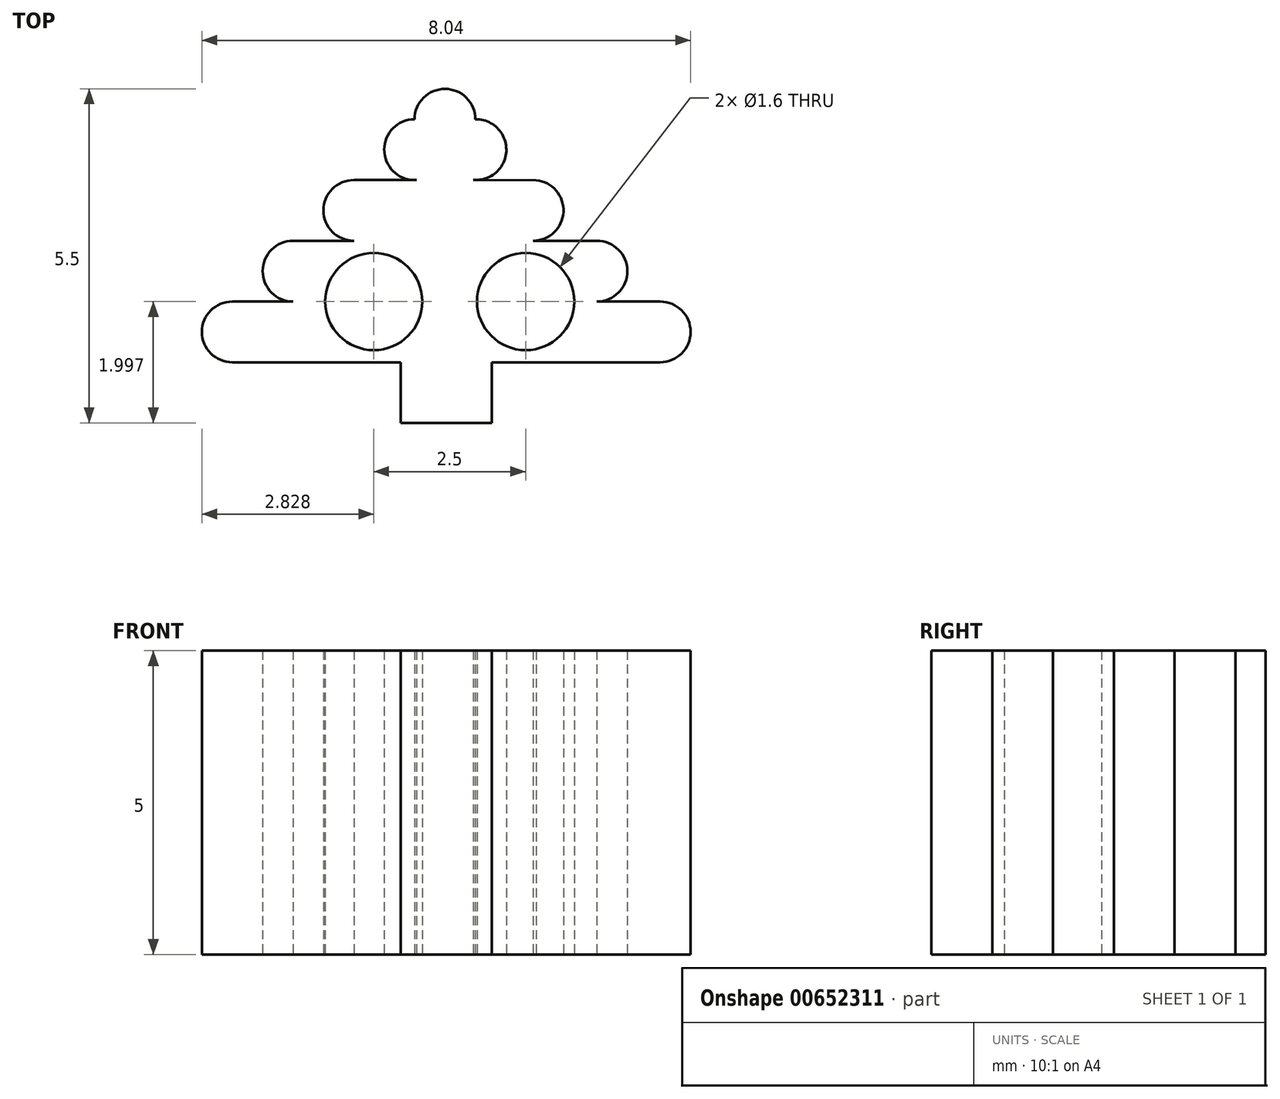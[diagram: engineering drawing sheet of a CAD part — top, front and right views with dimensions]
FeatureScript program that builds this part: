
annotation { "Feature Type Name" : "Feature", "Feature Type Description" : "" }
export const myFeature = defineFeature(function(context is Context, id is Id, definition is map)
    precondition{}
    {
        {
            var Q0;
            Q0=qCreatedBy(makeId("Top.planeOp"),FACE);
            var sketch = newSketch(context, id + "F0", { "sketchPlane" : qUnion([Q0])});
            skPoint(sketch, "E0.center.orphan", {"position": v(-33.1, 9.9) * mm});
            skPoint(sketch, "E1.center.orphan", {"position": v(-34.2, 9.9) * mm});
            skPoint(sketch, "E2.center.orphan", {"position": v(-35.15, 9.9) * mm});
            skPoint(sketch, "E3.center.orphan", {"position": v(-38.15, 9.9) * mm});
            skPoint(sketch, "E4.center.orphan", {"position": v(-36.15, 9.9) * mm});
            skPoint(sketch, "E4.start.orphan", {"position": v(-37.15, 9.9) * mm});
            skPoint(sketch, "E5.center.orphan", {"position": v(-39.15, 9.9) * mm});
            skPoint(sketch, "E5.end.orphan", {"position": v(-39.15, 8.9) * mm});
            skPoint(sketch, "E5.start.orphan", {"position": v(-39.15, 10.9) * mm});
            skPoint(sketch, "E6.center.orphan", {"position": v(-32.1, 9.9) * mm});
            skArc(sketch, "E7", {"start": v(-39.15, 10.4) * mm, "mid": v(-39.65, 9.9) * mm, "end": v(-39.15, 9.4) * mm});
            skArc(sketch, "E8", {"start": v(-32.1, 9.4) * mm, "mid": v(-31.6, 9.9) * mm, "end": v(-32.1, 10.4) * mm});
            skLineSegment(sketch, "E9", {"start": v(-32.1, 9.4) * mm, "end": v(-34.6, 9.4) * mm});
            skLineSegment(sketch, "E10", {"start": v(-32.1, 10.4) * mm, "end": v(-33.15, 10.4) * mm});
            skArc(sketch, "E11", {"start": v(-38.15, 11.4) * mm, "mid": v(-38.65, 10.9) * mm, "end": v(-38.15, 10.4) * mm});
            skArc(sketch, "E12", {"start": v(-33.15, 10.4) * mm, "mid": v(-32.65, 10.9) * mm, "end": v(-33.15, 11.4) * mm});
            skLineSegment(sketch, "E13", {"start": v(-38.15, 11.4) * mm, "end": v(-37.15, 11.4) * mm});
            skArc(sketch, "E14", {"start": v(-37.15, 12.4) * mm, "mid": v(-37.65, 11.9) * mm, "end": v(-37.15, 11.4) * mm});
            skArc(sketch, "E15", {"start": v(-36.12, 12.4) * mm, "mid": v(-36.15, 12.4) * mm, "end": v(-36.18, 12.4) * mm});
            skArc(sketch, "E16", {"start": v(-34.2, 11.4) * mm, "mid": v(-33.7, 11.93) * mm, "end": v(-34.25, 12.4) * mm});
            skLineSegment(sketch, "E17", {"start": v(-37.15, 12.4) * mm, "end": v(-36.12, 12.4) * mm});
            skArc(sketch, "E18.trimOffspring", {"start": v(-35.1, 12.4) * mm, "mid": v(-35.14, 12.4) * mm, "end": v(-35.18, 12.4) * mm});
            skLineSegment(sketch, "E19", {"start": v(-35.14, 12.4) * mm, "end": v(-35.14, 12.4) * mm});
            skArc(sketch, "E20", {"start": v(-36.15, 13.4) * mm, "mid": v(-36.65, 12.9) * mm, "end": v(-36.15, 12.4) * mm});
            skArc(sketch, "E21", {"start": v(-35.14, 12.4) * mm, "mid": v(-34.64, 12.91) * mm, "end": v(-35.15, 13.4) * mm});
            skLineSegment(sketch, "E22.trimOffspring", {"start": v(-35.18, 12.4) * mm, "end": v(-34.15, 12.4) * mm});
            skLineSegment(sketch, "E23.trimOffspring", {"start": v(-34.2, 11.4) * mm, "end": v(-33.15, 11.4) * mm});
            skLineSegment(sketch, "E24.trimOffspring", {"start": v(-38.15, 10.4) * mm, "end": v(-39.15, 10.4) * mm});
            skLineSegment(sketch, "E25", {"start": v(-35.65, 13.4) * mm, "end": v(-35.65, 13.4) * mm});
            skPoint(sketch, "E25.endSnap0", {"position": v(-35.65, 13.4) * mm});
            skPoint(sketch, "E26.center.orphan", {"position": v(-35.65, 13.9) * mm});
            skArc(sketch, "E27", {"start": v(-35.15, 13.4) * mm, "mid": v(-35.65, 13.9) * mm, "end": v(-36.15, 13.4) * mm});
            skLineSegment(sketch, "E28.trimOffspring", {"start": v(-36.65, 9.4) * mm, "end": v(-39.15, 9.4) * mm});
            skLineSegment(sketch, "E29", {"start": v(-36.65, 9.4) * mm, "end": v(-36.38, 9.4) * mm});
            skPoint(sketch, "E30.start.orphan", {"position": v(-39.65, 9.9) * mm});
            skPoint(sketch, "E31.start.orphan", {"position": v(-31.6, 9.9) * mm});
            skLineSegment(sketch, "E32", {"start": v(-36.38, 9.4) * mm, "end": v(-36.38, 8.4) * mm});
            skLineSegment(sketch, "E33", {"start": v(-36.38, 8.4) * mm, "end": v(-34.88, 8.4) * mm});
            skLineSegment(sketch, "E34", {"start": v(-34.88, 8.4) * mm, "end": v(-34.88, 9.4) * mm});
            skLineSegment(sketch, "E35.trimOffspring", {"start": v(-34.88, 9.4) * mm, "end": v(-34.6, 9.4) * mm});
            skPoint(sketch, "E36.center.orphan", {"position": v(-36.15, 11.4) * mm});
            skCircle(sketch, "E37", {"center": v(-36.82, 10.4) * mm, "radius": 0.8 * mm});
            skCircle(sketch, "E38", {"center": v(-34.32, 10.4) * mm, "radius": 0.8 * mm});
            skSolve(sketch);
        }
        {
            var Q0;
            Q0=makeQuery(id+"F0.imprint","IMPRINT",FACE,{"disambiguationData":[TD([[makeQuery(id+"F0.imprint","IMPRINT",EDGE,{"derivedFrom":sQuery(id+"F0.wireOp",EDGE,"E7")}),1.0]])]});
            extrude(context, id + "F1", {"entities" : qUnion([Q0]), "depth" : 5 * mm, "offsetDistance" : 25 * mm});
        }
    });
